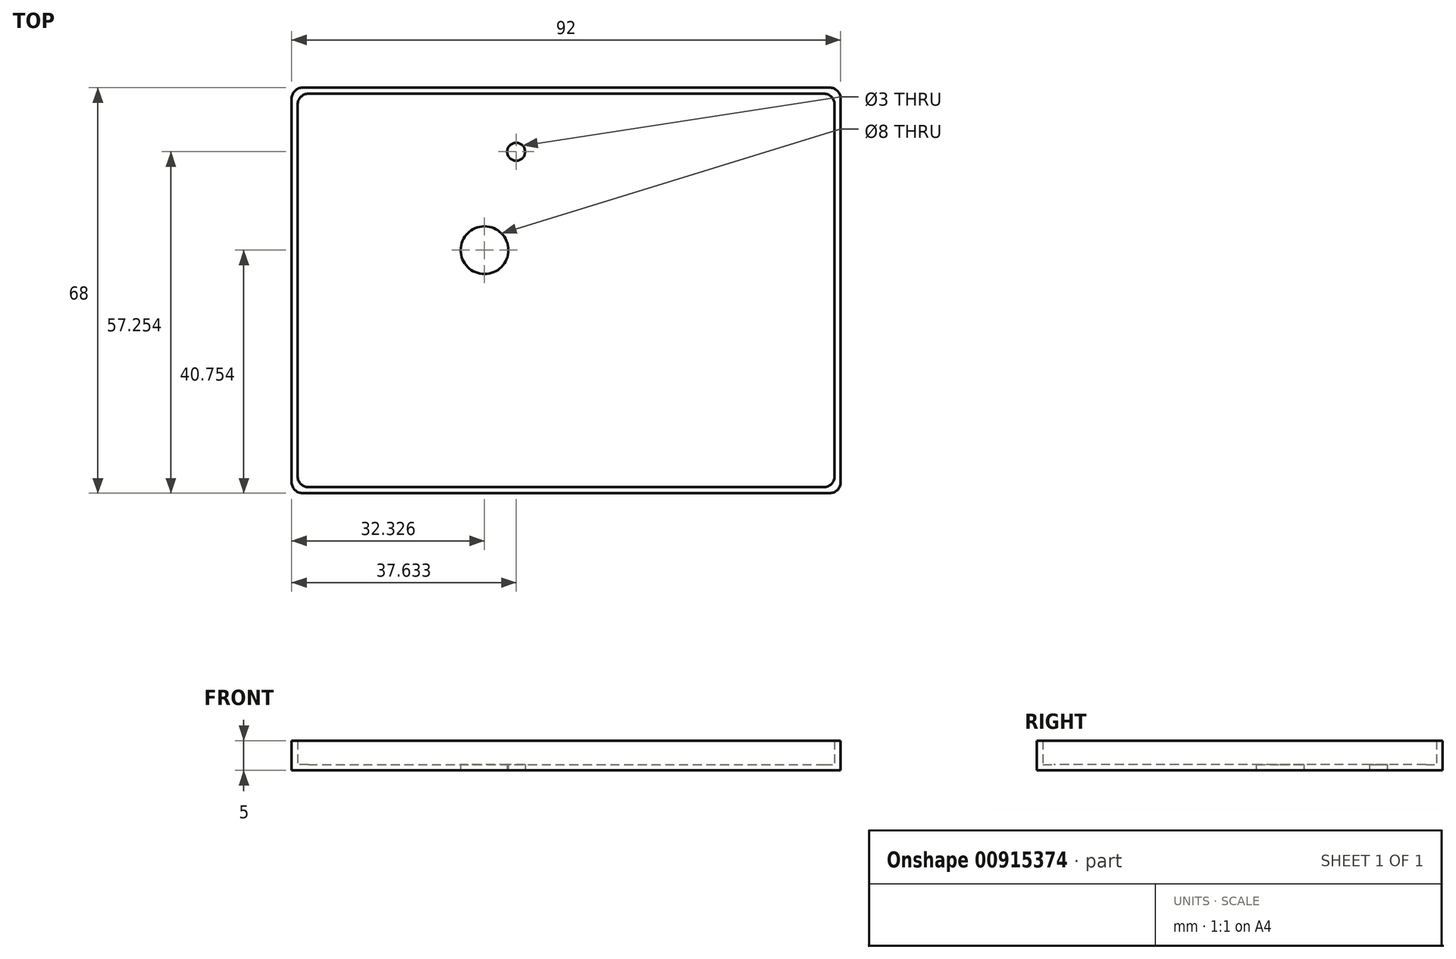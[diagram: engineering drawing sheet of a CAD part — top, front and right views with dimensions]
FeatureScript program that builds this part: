
annotation { "Feature Type Name" : "Feature", "Feature Type Description" : "" }
export const myFeature = defineFeature(function(context is Context, id is Id, definition is map)
    precondition{}
    {
        {
            var Q0;
            Q0=qCreatedBy(makeId("Top.planeOp"),FACE);
            var sketch = newSketch(context, id + "F0", { "sketchPlane" : qUnion([Q0])});
            skLineSegment(sketch, "E0.bottom", {"start": v(-45, 33) * mm, "end": v(45, 33) * mm});
            skLineSegment(sketch, "E0.top", {"start": v(-45, -33) * mm, "end": v(45, -33) * mm});
            skLineSegment(sketch, "E0.left", {"start": v(-45, 33) * mm, "end": v(-45, -33) * mm});
            skLineSegment(sketch, "E0.right", {"start": v(45, 33) * mm, "end": v(45, -33) * mm});
            skLineSegment(sketch, "E1.bottom", {"start": v(-46, 34) * mm, "end": v(46, 34) * mm});
            skLineSegment(sketch, "E1.top", {"start": v(-46, -34) * mm, "end": v(46, -34) * mm});
            skLineSegment(sketch, "E1.left", {"start": v(-46, 34) * mm, "end": v(-46, -34) * mm});
            skLineSegment(sketch, "E1.right", {"start": v(46, 34) * mm, "end": v(46, -34) * mm});
            skSolve(sketch);
        }
        {
            var Q0;
            Q0=qCreatedBy(makeId("Top.planeOp"),FACE);
            var sketch = newSketch(context, id + "F1", { "sketchPlane" : qUnion([Q0])});
            skLineSegment(sketch, "E2.bottom", {"start": v(-44.7, 32.3) * mm, "end": v(41.3, 32.3) * mm});
            skLineSegment(sketch, "E2.top", {"start": v(-44.7, -29.7) * mm, "end": v(41.3, -29.7) * mm});
            skLineSegment(sketch, "E2.left", {"start": v(-44.7, 32.3) * mm, "end": v(-44.7, -29.7) * mm});
            skLineSegment(sketch, "E2.right", {"start": v(41.3, 32.3) * mm, "end": v(41.3, -29.7) * mm});
            skLineSegment(sketch, "E3.bottom", {"start": v(-42.67, 29.75) * mm, "end": v(10.33, 29.75) * mm});
            skLineSegment(sketch, "E3.top", {"start": v(-42.67, -27.25) * mm, "end": v(10.33, -27.25) * mm});
            skLineSegment(sketch, "E3.left", {"start": v(-42.67, 29.75) * mm, "end": v(-42.67, -27.25) * mm});
            skLineSegment(sketch, "E3.right", {"start": v(10.33, 29.75) * mm, "end": v(10.33, -27.25) * mm});
            skLineSegment(sketch, "E4.bottom", {"start": v(13.63, 26.7) * mm, "end": v(39.63, 26.7) * mm});
            skLineSegment(sketch, "E4.top", {"start": v(13.63, -25.3) * mm, "end": v(39.63, -25.3) * mm});
            skLineSegment(sketch, "E4.left", {"start": v(13.63, 26.7) * mm, "end": v(13.63, -25.3) * mm});
            skLineSegment(sketch, "E4.right", {"start": v(39.63, 26.7) * mm, "end": v(39.63, -25.3) * mm});
            skCircle(sketch, "E5", {"center": v(4.23, 23.65) * mm, "radius": 1.1 * mm});
            skCircle(sketch, "E6", {"center": v(7.23, -21.25) * mm, "radius": 2 * mm});
            skCircle(sketch, "E7", {"center": v(-39.62, -20.7) * mm, "radius": 1.05 * mm});
            skLineSegment(sketch, "E8.bottom", {"start": v(-45.7, 33.3) * mm, "end": v(42.3, 33.3) * mm});
            skLineSegment(sketch, "E8.top", {"start": v(-45.7, -30.7) * mm, "end": v(42.3, -30.7) * mm});
            skLineSegment(sketch, "E8.left", {"start": v(-45.7, 33.3) * mm, "end": v(-45.7, -30.7) * mm});
            skLineSegment(sketch, "E8.right", {"start": v(42.3, 33.3) * mm, "end": v(42.3, -30.7) * mm});
            skCircle(sketch, "E9", {"center": v(-13.67, 6.75) * mm, "radius": 4 * mm});
            skCircle(sketch, "E10", {"center": v(-8.37, 23.25) * mm, "radius": 1.5 * mm});
            skSolve(sketch);
        }
        {
            var Q0;
            Q0=makeQuery(id+"F0.imprint","IMPRINT",FACE,{"disambiguationData":[TD([[makeQuery(id+"F0.imprint","IMPRINT",EDGE,{"derivedFrom":sQuery(id+"F0.wireOp",EDGE,"E0.bottom")}),1.0]])]});
            extrude(context, id + "F2", {"entities" : qUnion([Q0]), "depth" : 5 * mm, "offsetDistance" : 25.4 * mm});
        }
        {
            var Q0;
            Q0=makeQuery(id+"F0.imprint","IMPRINT",FACE,{"disambiguationData":[TD([[makeQuery(id+"F0.imprint","IMPRINT",EDGE,{"derivedFrom":sQuery(id+"F0.wireOp",EDGE,"E0.bottom")}),-1.0]])]});
            extrude(context, id + "F3", {"entities" : qUnion([Q0]), "operationType" : NewBodyOperationType.ADD, "depth" : 1 * mm, "offsetDistance" : 25.4 * mm});
        }
        {
            var Q0;
            Q0=makeQuery(id+"F1.imprint","IMPRINT",FACE,{"disambiguationData":[TD([[makeQuery(id+"F1.imprint","IMPRINT",EDGE,{"derivedFrom":sQuery(id+"F1.wireOp",EDGE,"E9")}),1.0]])]});
            var Q1;
            Q1=makeQuery(id+"F1.imprint","IMPRINT",FACE,{"disambiguationData":[TD([[makeQuery(id+"F1.imprint","IMPRINT",EDGE,{"derivedFrom":sQuery(id+"F1.wireOp",EDGE,"E10")}),1.0]])]});
            extrude(context, id + "F4", {"entities" : qUnion([Q0, Q1]), "operationType" : NewBodyOperationType.REMOVE, "depth" : 2.54 * mm, "offsetDistance" : 25.4 * mm});
        }
        {
            var Q0;
            Q0=makeQuery(id+"F2.opExtrude","SWEPT_EDGE",EDGE,{"disambiguationData":[OSD([sQuery(id+"F0.wireOp",EDGE,"E0.bottom"),sQuery(id+"F0.wireOp",EDGE,"E0.left")])]});
            var Q1;
            Q1=makeQuery(id+"F2.opExtrude","SWEPT_EDGE",EDGE,{"disambiguationData":[OSD([sQuery(id+"F0.wireOp",EDGE,"E0.bottom"),sQuery(id+"F0.wireOp",EDGE,"E0.right")])]});
            var Q2;
            Q2=makeQuery(id+"F2.opExtrude","SWEPT_EDGE",EDGE,{"disambiguationData":[OSD([sQuery(id+"F0.wireOp",EDGE,"E0.top"),sQuery(id+"F0.wireOp",EDGE,"E0.left")])]});
            var Q3;
            Q3=makeQuery(id+"F2.opExtrude","SWEPT_EDGE",EDGE,{"disambiguationData":[OSD([sQuery(id+"F0.wireOp",EDGE,"E0.top"),sQuery(id+"F0.wireOp",EDGE,"E0.right")])]});
            var Q4;
            Q4=makeQuery(id+"F2.opExtrude","SWEPT_EDGE",EDGE,{"disambiguationData":[OSD([sQuery(id+"F0.wireOp",EDGE,"E1.top"),sQuery(id+"F0.wireOp",EDGE,"E1.right")])]});
            var Q5;
            Q5=makeQuery(id+"F2.opExtrude","SWEPT_EDGE",EDGE,{"disambiguationData":[OSD([sQuery(id+"F0.wireOp",EDGE,"E1.top"),sQuery(id+"F0.wireOp",EDGE,"E1.left")])]});
            var Q6;
            Q6=makeQuery(id+"F2.opExtrude","SWEPT_EDGE",EDGE,{"disambiguationData":[OSD([sQuery(id+"F0.wireOp",EDGE,"E1.bottom"),sQuery(id+"F0.wireOp",EDGE,"E1.left")])]});
            var Q7;
            Q7=makeQuery(id+"F2.opExtrude","SWEPT_EDGE",EDGE,{"disambiguationData":[OSD([sQuery(id+"F0.wireOp",EDGE,"E1.bottom"),sQuery(id+"F0.wireOp",EDGE,"E1.right")])]});
            fillet(context, id + "F5", {"entities" : qUnion([Q0, Q1, Q2, Q3, Q4, Q5, Q6, Q7]), "radius" : 1.83 * mm, "tangentPropagation" : true, "allowEdgeOverflow" : false});
        }
    });
